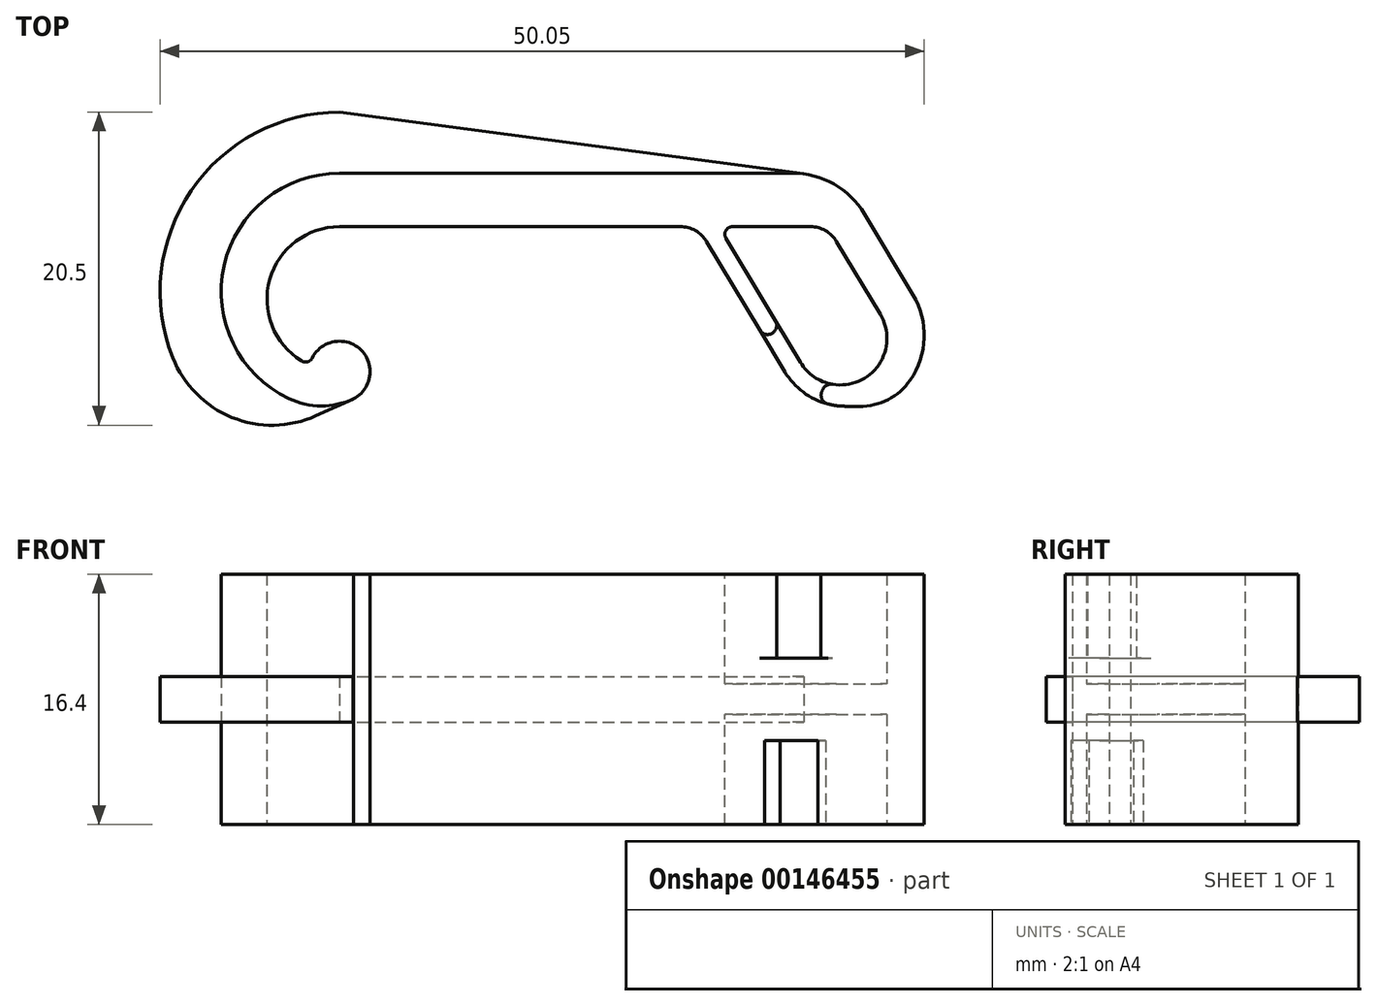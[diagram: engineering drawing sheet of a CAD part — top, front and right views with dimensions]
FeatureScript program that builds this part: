
annotation { "Feature Type Name" : "Feature", "Feature Type Description" : "" }
export const myFeature = defineFeature(function(context is Context, id is Id, definition is map)
    precondition{}
    {
        {
            var Q0;
            Q0=qCreatedBy(makeId("Top.planeOp"),FACE);
            var sketch = newSketch(context, id + "F0", { "sketchPlane" : qUnion([Q0])});
            skLineSegment(sketch, "E0", {"start": v(-40.2, 9.56) * mm, "end": v(-7.7, 9.56) * mm});
            skLineSegment(sketch, "E1", {"start": v(-7.7, 9.56) * mm, "end": v(-3.06, 1.84) * mm});
            skArc(sketch, "E2", {"start": v(-40.2, 9.56) * mm, "mid": v(-47.45, 2.3) * mm, "end": v(-40.2, -4.94) * mm});
            skArc(sketch, "E3", {"start": v(-3.06, 1.84) * mm, "mid": v(-4.65, -4.54) * mm, "end": v(-11.04, -2.95) * mm});
            skLineSegment(sketch, "E4", {"start": v(-3.06, 1.84) * mm, "end": v(-11.72, -3.36) * mm, "construction": true});
            skLineSegment(sketch, "E5", {"start": v(-11.04, -2.95) * mm, "end": v(-16.75, 6.56) * mm});
            skLineSegment(sketch, "E6", {"start": v(-40.2, 9.56) * mm, "end": v(-40.2, -4.94) * mm, "construction": true});
            skLineSegment(sketch, "E7", {"start": v(-40.2, 6.56) * mm, "end": v(-16.75, 6.56) * mm});
            skLineSegment(sketch, "E8.0", {"start": v(-8.23, 6.56) * mm, "end": v(-4.78, 0.81) * mm});
            skLineSegment(sketch, "E9.0", {"start": v(-10, -2.33) * mm, "end": v(-15.35, 6.56) * mm});
            skLineSegment(sketch, "E10.trimOffspring", {"start": v(-15.35, 6.56) * mm, "end": v(-8.23, 6.56) * mm});
            skArc(sketch, "E11", {"start": v(-40.2, -4.94) * mm, "mid": v(-38.64, -1.69) * mm, "end": v(-42.15, -2.52) * mm});
            skArc(sketch, "E12", {"start": v(-40.2, 6.56) * mm, "mid": v(-44.84, 2.8) * mm, "end": v(-42.15, -2.52) * mm});
            skArc(sketch, "E13", {"start": v(-10, -2.33) * mm, "mid": v(-5.82, -3.37) * mm, "end": v(-4.78, 0.81) * mm});
            skSolve(sketch);
        }
        {
            var Q0;
            Q0=qSketchRegion(id+"F0",true);
            extrude(context, id + "F1", {"entities" : qUnion([Q0]), "endBound" : BoundingType.SYMMETRIC, "depth" : 16.4 * mm});
        }
        {
            var Q0;
            Q0=makeQuery(id+"F0.imprint","IMPRINT",FACE,{"disambiguationData":[TD([[makeQuery(id+"F0.imprint","IMPRINT",EDGE,{"derivedFrom":sQuery(id+"F0.wireOp",EDGE,"E8.0")}),-1.0]])]});
            extrude(context, id + "F2", {"entities" : qUnion([Q0]), "operationType" : NewBodyOperationType.ADD, "endBound" : BoundingType.SYMMETRIC, "depth" : 2 * mm});
        }
        {
            var Q0;
            Q0=makeQuery(id+"F1.opExtrude","CAP_FACE",FACE,{"disambiguationData":[OSD([sQuery(id+"F0.wireOp",EDGE,"E0"),sQuery(id+"F0.wireOp",EDGE,"E1"),sQuery(id+"F0.wireOp",EDGE,"E2"),sQuery(id+"F0.wireOp",EDGE,"E3"),sQuery(id+"F0.wireOp",EDGE,"E5"),sQuery(id+"F0.wireOp",EDGE,"E7"),sQuery(id+"F0.wireOp",EDGE,"E8.0"),sQuery(id+"F0.wireOp",EDGE,"E9.0"),sQuery(id+"F0.wireOp",EDGE,"E10.trimOffspring"),sQuery(id+"F0.wireOp",EDGE,"E11"),sQuery(id+"F0.wireOp",EDGE,"E12"),sQuery(id+"F0.wireOp",EDGE,"E13")])],"isStart":false});
            var sketch = newSketch(context, id + "F3", { "sketchPlane" : qUnion([Q0])});
            skPoint(sketch, "E14", {"position": v(-7.05, -0.55) * mm});
            skLineSegment(sketch, "E15", {"start": v(-7.05, -0.55) * mm, "end": v(-9.8, -7.06) * mm});
            skLineSegment(sketch, "E16", {"start": v(-8.38, 1.67) * mm, "end": v(-13.29, -1.28) * mm});
            skLineSegment(sketch, "E17", {"start": v(-8.38, 1.67) * mm, "end": v(-7.05, -0.55) * mm});
            skLineSegment(sketch, "E18", {"start": v(-13.29, -1.28) * mm, "end": v(-9.8, -7.06) * mm});
            skArc(sketch, "E19.0", {"start": v(-3.02, 1.77) * mm, "mid": v(-4.72, -4.58) * mm, "end": v(-11.08, -2.88) * mm, "construction": true});
            skLineSegment(sketch, "E20", {"start": v(-7.05, -0.55) * mm, "end": v(-14, 11) * mm, "construction": true});
            skLineSegment(sketch, "E21.0", {"start": v(-40.2, 9.56) * mm, "end": v(-8.2, 9.56) * mm, "construction": true});
            skPoint(sketch, "E22", {"position": v(-14.3, 9.56) * mm});
            skSolve(sketch);
        }
        {
            var Q0;
            Q0=qSketchRegion(id+"F3",true);
            extrude(context, id + "F4", {"entities" : qUnion([Q0]), "operationType" : NewBodyOperationType.REMOVE, "oppositeDirection" : true, "depth" : 5.5 * mm});
        }
        {
            var Q0;
            Q0=makeQuery(id+"F1.opExtrude","CAP_FACE",FACE,{"disambiguationData":[OSD([sQuery(id+"F0.wireOp",EDGE,"E0"),sQuery(id+"F0.wireOp",EDGE,"E1"),sQuery(id+"F0.wireOp",EDGE,"E2"),sQuery(id+"F0.wireOp",EDGE,"E3"),sQuery(id+"F0.wireOp",EDGE,"E5"),sQuery(id+"F0.wireOp",EDGE,"E7"),sQuery(id+"F0.wireOp",EDGE,"E8.0"),sQuery(id+"F0.wireOp",EDGE,"E9.0"),sQuery(id+"F0.wireOp",EDGE,"E10.trimOffspring"),sQuery(id+"F0.wireOp",EDGE,"E11"),sQuery(id+"F0.wireOp",EDGE,"E12"),sQuery(id+"F0.wireOp",EDGE,"E13")])],"isStart":true});
            var sketch = newSketch(context, id + "F14", { "sketchPlane" : qUnion([Q0])});
            skLineSegment(sketch, "E23.0", {"start": v(-8.72, -1.46) * mm, "end": v(-13.42, 1.36) * mm});
            skLineSegment(sketch, "E24.0", {"start": v(-13.32, 1.21) * mm, "end": v(-10.9, 5.24) * mm});
            skLineSegment(sketch, "E25.0", {"start": v(-7.27, 1.06) * mm, "end": v(-9.48, 6.28) * mm});
            skLineSegment(sketch, "E26.0", {"start": v(-8.37, -1.65) * mm, "end": v(-6.7, 1.12) * mm});
            skSolve(sketch);
        }
        {
            var Q0;
            {var subQ0=makeQuery(id+"F1.opExtrude","CAP_EDGE",EDGE,{"disambiguationData":[OSD([sQuery(id+"F0.wireOp",EDGE,"E5")])],"isStart":true});var subQ5=sQuery(id+"F14.wireOp",EDGE,"E23.0");var subQ6=makeQuery(id+"F14.imprint","INTERSECT",VERTEX,{"derivedFrom":[subQ0,subQ5]});Q0=makeQuery(id+"F14.imprint","IMPRINT",FACE,{"disambiguationData":[TD([[makeQuery(id+"F14.imprint","IMPRINT",EDGE,{"disambiguationData":[TD([[subQ6,1.0]])],"derivedFrom":subQ5}),-1.0]])]});}
            extrude(context, id + "F15", {"entities" : qUnion([Q0]), "operationType" : NewBodyOperationType.REMOVE, "oppositeDirection" : true, "depth" : 5.5 * mm});
        }
        {
            var Q0;
            Q0=makeQuery(id+"F1.opExtrude","SWEPT_EDGE",EDGE,{"disambiguationData":[OSD([sQuery(id+"F0.wireOp",EDGE,"E5"),sQuery(id+"F0.wireOp",EDGE,"E7")])]});
            fillet(context, id + "F5", {"entities" : qUnion([Q0]), "radius" : 2 * mm, "tangentPropagation" : true, "allowEdgeOverflow" : false});
        }
        {
            var Q0;
            {var subQ0=sQuery(id+"F0.wireOp",EDGE,"E13");var subQ1=sQuery(id+"F0.wireOp",EDGE,"E10.trimOffspring");var subQ2=sQuery(id+"F0.wireOp",EDGE,"E9.0");var subQ3=sQuery(id+"F0.wireOp",EDGE,"E8.0");Q0=makeQuery(id+"F2.boolean.opBoolean","SPLIT",EDGE,{"disambiguationData":[TD([makeQuery(id+"F2.opExtrude","CAP_FACE",FACE,{"disambiguationData":[OSD([subQ3,subQ2,subQ1,subQ0])],"isStart":true})])],"derivedFrom":makeQuery(id+"F1.opExtrude","SWEPT_EDGE",EDGE,{"disambiguationData":[OSD([subQ2,subQ1])]})});}
            var Q1;
            {var subQ0=sQuery(id+"F0.wireOp",EDGE,"E13");var subQ1=sQuery(id+"F0.wireOp",EDGE,"E10.trimOffspring");var subQ2=sQuery(id+"F0.wireOp",EDGE,"E9.0");var subQ3=sQuery(id+"F0.wireOp",EDGE,"E8.0");Q1=makeQuery(id+"F2.boolean.opBoolean","SPLIT",EDGE,{"disambiguationData":[TD([makeQuery(id+"F2.opExtrude","CAP_FACE",FACE,{"disambiguationData":[OSD([subQ3,subQ2,subQ1,subQ0])],"isStart":false})])],"derivedFrom":makeQuery(id+"F1.opExtrude","SWEPT_EDGE",EDGE,{"disambiguationData":[OSD([subQ2,subQ1])]})});}
            fillet(context, id + "F16", {"entities" : qUnion([Q0, Q1]), "radius" : 0.5 * mm, "tangentPropagation" : true, "allowEdgeOverflow" : false});
        }
        {
            var Q0;
            {var subQ0=sQuery(id+"F0.wireOp",EDGE,"E13");var subQ1=sQuery(id+"F0.wireOp",EDGE,"E10.trimOffspring");var subQ2=sQuery(id+"F0.wireOp",EDGE,"E9.0");var subQ3=sQuery(id+"F0.wireOp",EDGE,"E8.0");Q0=makeQuery(id+"F2.boolean.opBoolean","SPLIT",EDGE,{"disambiguationData":[TD([makeQuery(id+"F2.opExtrude","CAP_FACE",FACE,{"disambiguationData":[OSD([subQ3,subQ2,subQ1,subQ0])],"isStart":true})])],"derivedFrom":makeQuery(id+"F1.opExtrude","SWEPT_EDGE",EDGE,{"disambiguationData":[OSD([subQ3,subQ1])]})});}
            var Q1;
            {var subQ0=sQuery(id+"F0.wireOp",EDGE,"E13");var subQ1=sQuery(id+"F0.wireOp",EDGE,"E10.trimOffspring");var subQ2=sQuery(id+"F0.wireOp",EDGE,"E9.0");var subQ3=sQuery(id+"F0.wireOp",EDGE,"E8.0");Q1=makeQuery(id+"F2.boolean.opBoolean","SPLIT",EDGE,{"disambiguationData":[TD([makeQuery(id+"F2.opExtrude","CAP_FACE",FACE,{"disambiguationData":[OSD([subQ3,subQ2,subQ1,subQ0])],"isStart":false})])],"derivedFrom":makeQuery(id+"F1.opExtrude","SWEPT_EDGE",EDGE,{"disambiguationData":[OSD([subQ3,subQ1])]})});}
            fillet(context, id + "F17", {"entities" : qUnion([Q0, Q1]), "radius" : 2 * mm, "tangentPropagation" : true, "allowEdgeOverflow" : false});
        }
        {
            var Q0;
            Q0=makeQuery(id+"F1.opExtrude","SWEPT_EDGE",EDGE,{"disambiguationData":[OSD([sQuery(id+"F0.wireOp",EDGE,"E0"),sQuery(id+"F0.wireOp",EDGE,"E1")])]});
            fillet(context, id + "F18", {"entities" : qUnion([Q0]), "radius" : 5 * mm, "tangentPropagation" : true, "allowEdgeOverflow" : false});
        }
        {
            var Q0;
            Q0=makeQuery(id+"F1.opExtrude","SWEPT_EDGE",EDGE,{"disambiguationData":[OSD([sQuery(id+"F0.wireOp",EDGE,"E11"),sQuery(id+"F0.wireOp",EDGE,"E12")])]});
            fillet(context, id + "F19", {"entities" : qUnion([Q0]), "radius" : 0.5 * mm, "tangentPropagation" : true, "allowEdgeOverflow" : false});
        }
        {
            var Q0;
            Q0=makeQuery(id+"F4.boolean.opBoolean","INTERSECT",EDGE,{"derivedFrom":[makeQuery(id+"F1.opExtrude","SWEPT_FACE",FACE,{"disambiguationData":[OSD([sQuery(id+"F0.wireOp",EDGE,"E5")])]}),makeQuery(id+"F4.opExtrude","SWEPT_FACE",FACE,{"disambiguationData":[OSD([sQuery(id+"F3.wireOp",EDGE,"E16")])]})]});
            var Q1;
            {var subQ0=sQuery(id+"F0.wireOp",EDGE,"E13");var subQ1=sQuery(id+"F0.wireOp",EDGE,"E10.trimOffspring");var subQ2=sQuery(id+"F0.wireOp",EDGE,"E9.0");var subQ3=sQuery(id+"F0.wireOp",EDGE,"E8.0");Q1=makeQuery(id+"F4.boolean.opBoolean","INTERSECT",EDGE,{"derivedFrom":[makeQuery(id+"F2.boolean.opBoolean","SPLIT",FACE,{"disambiguationData":[TD([makeQuery(id+"F2.opExtrude","CAP_FACE",FACE,{"disambiguationData":[OSD([subQ3,subQ2,subQ1,subQ0])],"isStart":false})])],"derivedFrom":makeQuery(id+"F1.opExtrude","SWEPT_FACE",FACE,{"disambiguationData":[OSD([subQ2])]})}),makeQuery(id+"F4.opExtrude","SWEPT_FACE",FACE,{"disambiguationData":[OSD([sQuery(id+"F3.wireOp",EDGE,"E16")])]})]});}
            var Q2;
            {var subQ0=sQuery(id+"F0.wireOp",EDGE,"E13");var subQ1=sQuery(id+"F0.wireOp",EDGE,"E10.trimOffspring");var subQ2=sQuery(id+"F0.wireOp",EDGE,"E9.0");var subQ3=sQuery(id+"F0.wireOp",EDGE,"E8.0");Q2=makeQuery(id+"F4.boolean.opBoolean","INTERSECT",EDGE,{"derivedFrom":[makeQuery(id+"F2.boolean.opBoolean","SPLIT",FACE,{"disambiguationData":[TD([makeQuery(id+"F2.opExtrude","CAP_FACE",FACE,{"disambiguationData":[OSD([subQ3,subQ2,subQ1,subQ0])],"isStart":false})])],"derivedFrom":makeQuery(id+"F1.opExtrude","SWEPT_FACE",FACE,{"disambiguationData":[OSD([subQ0])]})}),makeQuery(id+"F4.opExtrude","SWEPT_FACE",FACE,{"disambiguationData":[OSD([sQuery(id+"F3.wireOp",EDGE,"E15")])]})]});}
            var Q3;
            Q3=makeQuery(id+"F4.boolean.opBoolean","INTERSECT",EDGE,{"derivedFrom":[makeQuery(id+"F1.opExtrude","SWEPT_FACE",FACE,{"disambiguationData":[OSD([sQuery(id+"F0.wireOp",EDGE,"E3")])]}),makeQuery(id+"F4.opExtrude","SWEPT_FACE",FACE,{"disambiguationData":[OSD([sQuery(id+"F3.wireOp",EDGE,"E15")])]})]});
            var Q4;
            Q4=makeQuery(id+"F15.boolean.opBoolean","COPY",EDGE,{"derivedFrom":makeQuery(id+"F15.opExtrude","SWEPT_EDGE",EDGE,{"disambiguationData":[OSD([sQuery(id+"F0.wireOp",EDGE,"E3"),sQuery(id+"F14.wireOp",EDGE,"E25.0")])]})});
            var Q5;
            Q5=makeQuery(id+"F15.boolean.opBoolean","COPY",EDGE,{"derivedFrom":makeQuery(id+"F15.opExtrude","SWEPT_EDGE",EDGE,{"disambiguationData":[OSD([sQuery(id+"F0.wireOp",EDGE,"E13"),sQuery(id+"F14.wireOp",EDGE,"E25.0")])]})});
            var Q6;
            Q6=makeQuery(id+"F15.boolean.opBoolean","COPY",EDGE,{"derivedFrom":makeQuery(id+"F15.opExtrude","SWEPT_EDGE",EDGE,{"disambiguationData":[OSD([sQuery(id+"F0.wireOp",EDGE,"E5"),sQuery(id+"F14.wireOp",EDGE,"E23.0")])]})});
            var Q7;
            Q7=makeQuery(id+"F15.boolean.opBoolean","COPY",EDGE,{"derivedFrom":makeQuery(id+"F15.opExtrude","SWEPT_EDGE",EDGE,{"disambiguationData":[OSD([sQuery(id+"F0.wireOp",EDGE,"E9.0"),sQuery(id+"F14.wireOp",EDGE,"E23.0")])]})});
            fillet(context, id + "F6", {"entities" : qUnion([Q0, Q1, Q2, Q3, Q4, Q5, Q6, Q7]), "radius" : 0.6 * mm, "tangentPropagation" : true, "allowEdgeOverflow" : false});
        }
        {
            var Q0;
            Q0=qCreatedBy(makeId("Top.planeOp"),FACE);
            var sketch = newSketch(context, id + "F7", { "sketchPlane" : qUnion([Q0])});
            skArc(sketch, "E27.0", {"start": v(-40.2, 9.56) * mm, "mid": v(-47.45, 2.3) * mm, "end": v(-40.2, -4.94) * mm});
            skLineSegment(sketch, "E28.0", {"start": v(-40.2, 9.56) * mm, "end": v(-10.53, 9.56) * mm});
            skArc(sketch, "E29.0", {"start": v(-6.24, 7.13) * mm, "mid": v(-8.07, 8.9) * mm, "end": v(-10.53, 9.56) * mm});
            skLineSegment(sketch, "E30.0", {"start": v(-6.24, 7.13) * mm, "end": v(-3.06, 1.84) * mm});
            skArc(sketch, "E31.0", {"start": v(-3.06, 1.84) * mm, "mid": v(-3.01, -2.86) * mm, "end": v(-7.1, -5.2) * mm});
            skLineSegment(sketch, "E32.0", {"start": v(-40.2, 10.06) * mm, "end": v(-10.53, 10.06) * mm});
            skArc(sketch, "E33.0", {"start": v(-5.81, 7.4) * mm, "mid": v(-7.82, 9.35) * mm, "end": v(-10.53, 10.06) * mm});
            skLineSegment(sketch, "E34.0", {"start": v(-5.81, 7.4) * mm, "end": v(-2.64, 2.1) * mm});
            skArc(sketch, "E35.0", {"start": v(-40.2, 10.06) * mm, "mid": v(-47.95, 2.54) * mm, "end": v(-40.67, -5.43) * mm});
            skLineSegment(sketch, "E36", {"start": v(-40.67, -5.43) * mm, "end": v(-39.29, -4.72) * mm});
            skArc(sketch, "E37.0", {"start": v(-40.2, -4.94) * mm, "mid": v(-39.73, -4.89) * mm, "end": v(-39.29, -4.72) * mm});
            skArc(sketch, "E38.0", {"start": v(-2.64, 2.1) * mm, "mid": v(-2.13, -2.06) * mm, "end": v(-4.88, -5.22) * mm});
            skLineSegment(sketch, "E39", {"start": v(-7.1, -5.2) * mm, "end": v(-4.88, -5.22) * mm});
            skSolve(sketch);
        }
        {
            var Q0;
            Q0=qSketchRegion(id+"F7",true);
            extrude(context, id + "F8", {"entities" : qUnion([Q0]), "operationType" : NewBodyOperationType.ADD, "endBound" : BoundingType.SYMMETRIC, "depth" : 16.4 * mm});
        }
        {
            var Q0;
            Q0=makeQuery(id+"F8.opExtrude","SWEPT_EDGE",EDGE,{"disambiguationData":[OSD([sQuery(id+"F7.wireOp",EDGE,"E35.0"),sQuery(id+"F7.wireOp",EDGE,"E36")])]});
            fillet(context, id + "F9", {"entities" : qUnion([Q0]), "radius" : 5 * mm, "tangentPropagation" : true, "allowEdgeOverflow" : false});
        }
        {
            var Q0;
            Q0=makeQuery(id+"F8.opExtrude","SWEPT_EDGE",EDGE,{"disambiguationData":[OSD([sQuery(id+"F7.wireOp",EDGE,"E38.0"),sQuery(id+"F7.wireOp",EDGE,"E39")])]});
            fillet(context, id + "F10", {"entities" : qUnion([Q0]), "radius" : 4 * mm, "tangentPropagation" : true, "allowEdgeOverflow" : false});
        }
        {
            var Q0;
            Q0=qCreatedBy(makeId("Top.planeOp"),FACE);
            var sketch = newSketch(context, id + "F11", { "sketchPlane" : qUnion([Q0])});
            skArc(sketch, "E40.0", {"start": v(-40.2, 14.06) * mm, "mid": v(-51.54, 5.4) * mm, "end": v(-46.16, -7.82) * mm});
            skArc(sketch, "E41.0", {"start": v(-43.51, -4.7) * mm, "mid": v(-41.42, -5.18) * mm, "end": v(-39.32, -4.74) * mm});
            skArc(sketch, "E42.0", {"start": v(-9.8, 10.01) * mm, "mid": v(-10.16, 10.05) * mm, "end": v(-10.53, 10.06) * mm});
            skLineSegment(sketch, "E43", {"start": v(-46.16, -7.82) * mm, "end": v(-39.32, -4.74) * mm});
            skArc(sketch, "E44.0", {"start": v(-40.2, 10.06) * mm, "mid": v(-47.76, 4) * mm, "end": v(-43.51, -4.7) * mm});
            skLineSegment(sketch, "E45.0", {"start": v(-40.2, 10.06) * mm, "end": v(-10.53, 10.06) * mm});
            skLineSegment(sketch, "E46", {"start": v(-40.2, 14.06) * mm, "end": v(-9.8, 10.01) * mm});
            skSolve(sketch);
        }
        {
            var Q0;
            Q0=qSketchRegion(id+"F11",true);
            extrude(context, id + "F12", {"entities" : qUnion([Q0]), "endBound" : BoundingType.SYMMETRIC, "depth" : 3 * mm});
        }
        {
            var Q0;
            Q0=makeQuery(id+"F12.opExtrude","SWEPT_EDGE",EDGE,{"disambiguationData":[OSD([sQuery(id+"F11.wireOp",EDGE,"E40.0"),sQuery(id+"F11.wireOp",EDGE,"E43")])]});
            fillet(context, id + "F13", {"entities" : qUnion([Q0]), "radius" : 7 * mm, "tangentPropagation" : true, "allowEdgeOverflow" : false});
        }
    });
